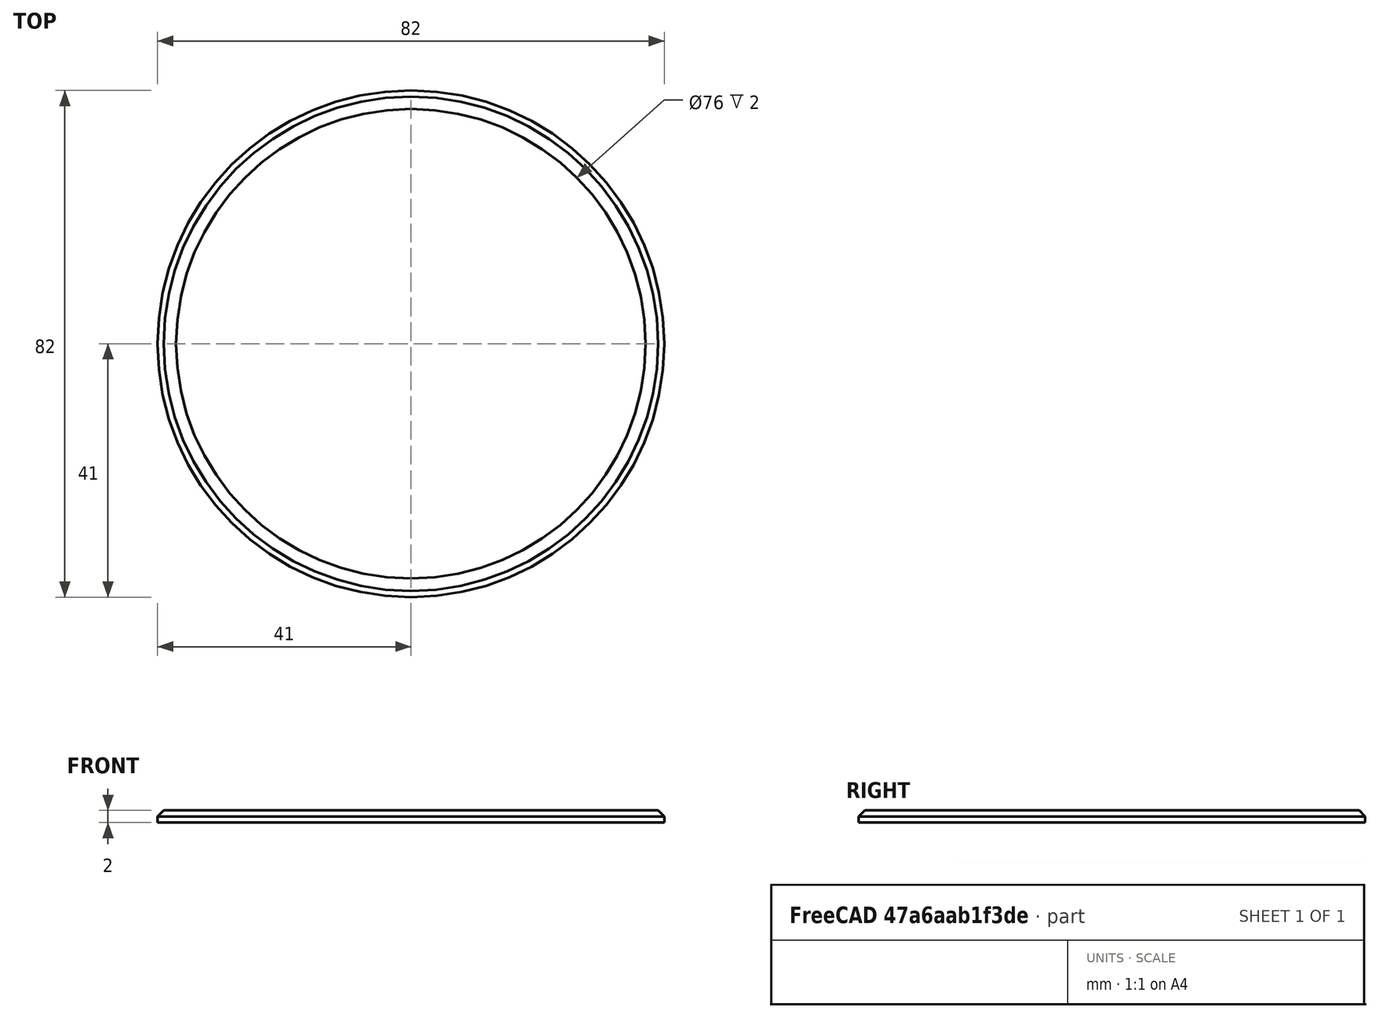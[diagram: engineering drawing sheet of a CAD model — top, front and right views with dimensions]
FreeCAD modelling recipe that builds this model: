
FCSTD DOCUMENT  (FreeCAD 0.19R24276 (Git))
Label: ring_add_76x82
License: All rights reserved
LicenseURL: http://en.wikipedia.org/wiki/All_rights_reserved
objects: Sketcher::SketchObject×1, PartDesign::Pad×1, PartDesign::Chamfer×1, PartDesign::Body×1
note: 6 computed .brp shape members not serialized (recipe doc carries the construction recipe); baked Part::Feature solids carry a one-line shape summary decoded from their .brp

FEATURE [Sketcher::SketchObject] Sketch
  FullyConstrained = true
  MapMode = 5
  Support = -> [XY_Plane]
  sketch-geometry (2):
    g0: Circle CenterX=0 CenterY=0 CenterZ=0 NormalX=0 NormalY=0 NormalZ=1 AngleXU=0 Radius=41
    g1: Circle CenterX=0 CenterY=0 CenterZ=0 NormalX=0 NormalY=0 NormalZ=1 AngleXU=0 Radius=38
  constraints (4):
    c: Coincident(g0,g-1)
    c: Coincident(g1,g0)
    c: Diameter(g0) = 82
    c: Diameter(g1) = 76
FEATURE [PartDesign::Pad] Pad
  Direction = (1,1,1)
  Length = 2
  Length2 = 100
  Profile = -> Sketch
  Type = 0
FEATURE [PartDesign::Chamfer] Chamfer
  Angle = 45
  Base = -> Pad [Edge3]
  BaseFeature = -> Pad
  ChamferType = 0
  FlipDirection = false
  Size = 1
  Size2 = 1
  SupportTransform = false
FEATURE [PartDesign::Body] Body
  Group = -> [Sketch,Pad,Chamfer]
  Origin = -> Origin
  Tip = -> Chamfer
